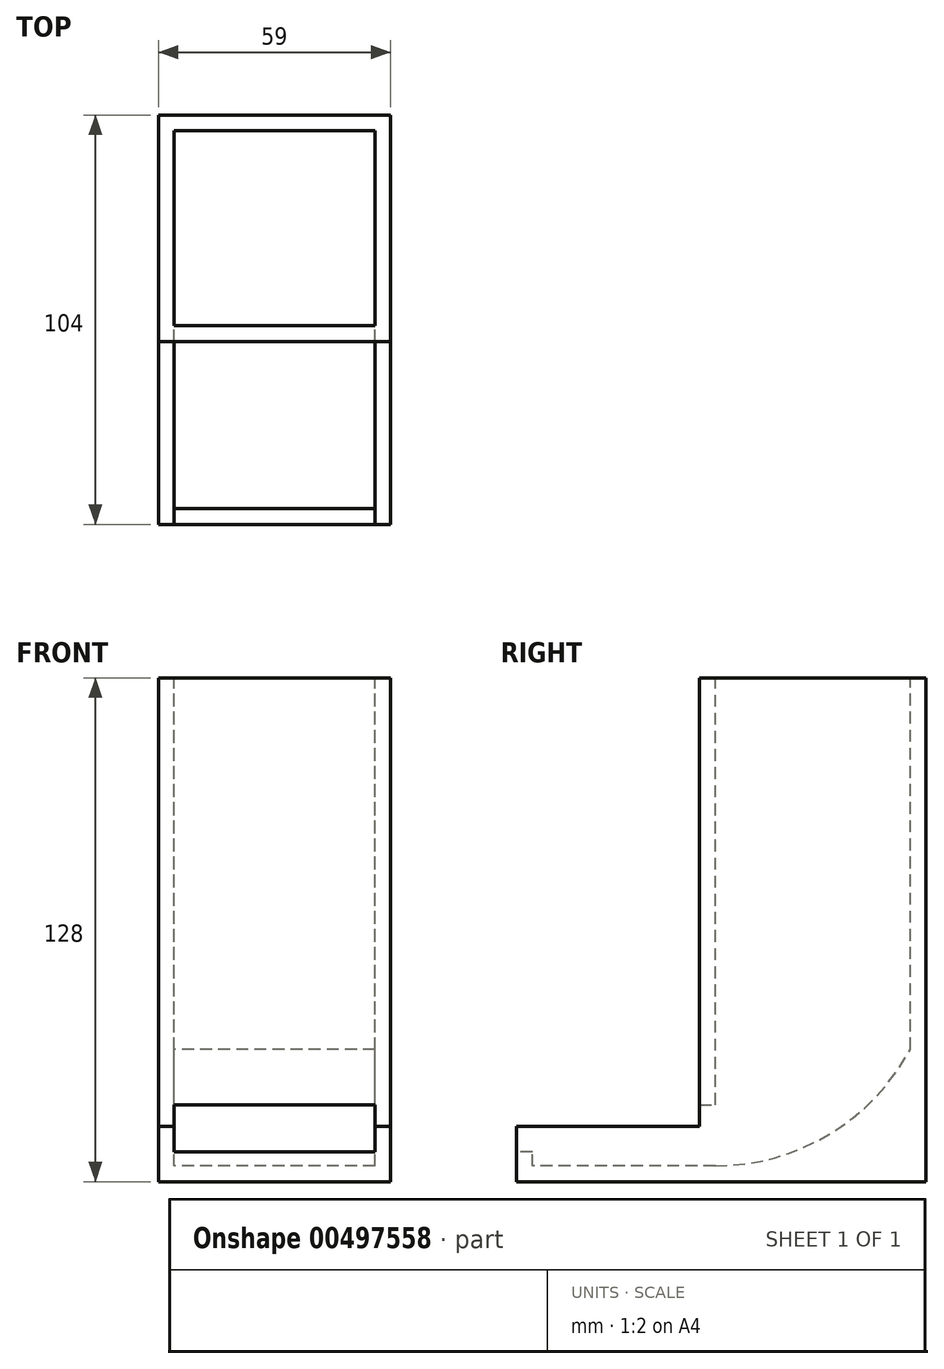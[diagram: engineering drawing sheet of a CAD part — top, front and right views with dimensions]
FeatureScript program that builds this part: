
annotation { "Feature Type Name" : "Feature", "Feature Type Description" : "" }
export const myFeature = defineFeature(function(context is Context, id is Id, definition is map)
    precondition{}
    {
        {
            var Q0;
            Q0=qCreatedBy(makeId("Right.planeOp"),FACE);
            var sketch = newSketch(context, id + "F0", { "sketchPlane" : qUnion([Q0])});
            skLineSegment(sketch, "E0", {"start": v(0, 0) * mm, "end": v(46.5, 0) * mm});
            skLineSegment(sketch, "E1", {"start": v(46.5, 0) * mm, "end": v(49.5, 0) * mm});
            skLineSegment(sketch, "E2", {"start": v(49.5, 0) * mm, "end": v(49.5, 120) * mm});
            skLineSegment(sketch, "E3", {"start": v(0, 0) * mm, "end": v(-46.5, 0) * mm});
            skLineSegment(sketch, "E4", {"start": v(-46.5, 0) * mm, "end": v(-46.5, 10) * mm});
            skLineSegment(sketch, "E5", {"start": v(-46.5, 10) * mm, "end": v(0, 10) * mm});
            skLineSegment(sketch, "E6", {"start": v(0, 15.5) * mm, "end": v(0, 120) * mm});
            skLineSegment(sketch, "E7", {"start": v(0, 120) * mm, "end": v(49.5, 120) * mm});
            skArc(sketch, "E8", {"start": v(0, 0) * mm, "mid": v(28.84, 7.97) * mm, "end": v(49.5, 29.6) * mm});
            skLineSegment(sketch, "E9", {"start": v(0, 0) * mm, "end": v(0, 10) * mm});
            skLineSegment(sketch, "E10", {"start": v(0, 15.5) * mm, "end": v(0, 56.18) * mm});
            skLineSegment(sketch, "E11", {"start": v(0, 10) * mm, "end": v(32, 10) * mm});
            skLineSegment(sketch, "E12.0", {"start": v(53.5, -4) * mm, "end": v(53.5, 124) * mm});
            skLineSegment(sketch, "E12.1", {"start": v(-4, 124) * mm, "end": v(53.5, 124) * mm});
            skLineSegment(sketch, "E12.2", {"start": v(-4, 15.5) * mm, "end": v(-4, 124) * mm});
            skLineSegment(sketch, "E13", {"start": v(-4, 15.5) * mm, "end": v(0, 15.5) * mm});
            skLineSegment(sketch, "E14.0", {"start": v(0, -4) * mm, "end": v(-50.5, -4) * mm});
            skLineSegment(sketch, "E14.1", {"start": v(0, -4) * mm, "end": v(46.5, -4) * mm});
            skLineSegment(sketch, "E14.2", {"start": v(46.5, -4) * mm, "end": v(53.5, -4) * mm});
            skLineSegment(sketch, "E15.0", {"start": v(-50.5, -4) * mm, "end": v(-50.5, 10) * mm});
            skLineSegment(sketch, "E16", {"start": v(-50.5, 10) * mm, "end": v(-46.5, 10) * mm});
            skLineSegment(sketch, "E17", {"start": v(-4, 15.5) * mm, "end": v(-4, 10) * mm});
            skLineSegment(sketch, "E18", {"start": v(-46.5, 3.51) * mm, "end": v(-50.5, 3.51) * mm});
            skLineSegment(sketch, "E19", {"start": v(0, 120) * mm, "end": v(0, 124) * mm});
            skLineSegment(sketch, "E20", {"start": v(49.5, 120) * mm, "end": v(49.5, 124) * mm});
            skSolve(sketch);
        }
        {
            var Q0;
            Q0=makeQuery(id+"F0.imprint","IMPRINT",FACE,{"disambiguationData":[TD([[makeQuery(id+"F0.imprint","IMPRINT",EDGE,{"derivedFrom":sQuery(id+"F0.wireOp",EDGE,"E0")}),-1.0]])]});
            var Q1;
            {var subQ4=sQuery(id+"F0.wireOp",EDGE,"E0");Q1=makeQuery(id+"F0.imprint","IMPRINT",FACE,{"disambiguationData":[TD([[makeQuery(id+"F0.imprint","IMPRINT",EDGE,{"derivedFrom":subQ4}),1.0]])]});}
            var Q2;
            {var subQ0=sQuery(id+"F0.wireOp",EDGE,"E9");Q2=makeQuery(id+"F0.imprint","IMPRINT",FACE,{"disambiguationData":[TD([[makeQuery(id+"F0.imprint","IMPRINT",EDGE,{"derivedFrom":subQ0}),-1.0]])]});}
            var Q3;
            Q3=makeQuery(id+"F0.imprint","IMPRINT",FACE,{"disambiguationData":[TD([[makeQuery(id+"F0.imprint","IMPRINT",EDGE,{"derivedFrom":sQuery(id+"F0.wireOp",EDGE,"E3")}),-1.0]])]});
            var Q4;
            Q4=makeQuery(id+"F0.imprint","IMPRINT",FACE,{"disambiguationData":[TD([[makeQuery(id+"F0.imprint","IMPRINT",EDGE,{"derivedFrom":sQuery(id+"F0.wireOp",EDGE,"E6")}),-1.0]])]});
            var Q5;
            {var subQ0=sQuery(id+"F0.wireOp",EDGE,"E16");Q5=makeQuery(id+"F0.imprint","IMPRINT",FACE,{"disambiguationData":[TD([[makeQuery(id+"F0.imprint","IMPRINT",EDGE,{"derivedFrom":subQ0}),-1.0]])]});}
            var Q6;
            Q6=makeQuery(id+"F0.imprint","IMPRINT",FACE,{"disambiguationData":[TD([[makeQuery(id+"F0.imprint","IMPRINT",EDGE,{"derivedFrom":sQuery(id+"F0.wireOp",EDGE,"E6")}),1.0]])]});
            var Q7;
            Q7=makeQuery(id+"F0.imprint","IMPRINT",FACE,{"disambiguationData":[TD([[makeQuery(id+"F0.imprint","IMPRINT",EDGE,{"derivedFrom":sQuery(id+"F0.wireOp",EDGE,"E7")}),1.0]])]});
            extrude(context, id + "F1", {"entities" : qUnion([Q0, Q1, Q2, Q3, Q4, Q5, Q6, Q7]), "oppositeDirection" : true, "depth" : 4 * mm, "offsetDistance" : 25 * mm});
        }
        {
            var Q0;
            Q0=makeQuery(id+"F0.imprint","IMPRINT",FACE,{"disambiguationData":[TD([[makeQuery(id+"F0.imprint","IMPRINT",EDGE,{"derivedFrom":sQuery(id+"F0.wireOp",EDGE,"E0")}),-1.0]])]});
            var Q1;
            {var subQ4=sQuery(id+"F0.wireOp",EDGE,"E0");Q1=makeQuery(id+"F0.imprint","IMPRINT",FACE,{"disambiguationData":[TD([[makeQuery(id+"F0.imprint","IMPRINT",EDGE,{"derivedFrom":subQ4}),1.0]])]});}
            var Q2;
            Q2=makeQuery(id+"F0.imprint","IMPRINT",FACE,{"disambiguationData":[TD([[makeQuery(id+"F0.imprint","IMPRINT",EDGE,{"derivedFrom":sQuery(id+"F0.wireOp",EDGE,"E6")}),-1.0]])]});
            var Q3;
            Q3=makeQuery(id+"F0.imprint","IMPRINT",FACE,{"disambiguationData":[TD([[makeQuery(id+"F0.imprint","IMPRINT",EDGE,{"derivedFrom":sQuery(id+"F0.wireOp",EDGE,"E3")}),-1.0]])]});
            var Q4;
            {var subQ0=sQuery(id+"F0.wireOp",EDGE,"E9");Q4=makeQuery(id+"F0.imprint","IMPRINT",FACE,{"disambiguationData":[TD([[makeQuery(id+"F0.imprint","IMPRINT",EDGE,{"derivedFrom":subQ0}),-1.0]])]});}
            var Q5;
            {var subQ0=sQuery(id+"F0.wireOp",EDGE,"E16");Q5=makeQuery(id+"F0.imprint","IMPRINT",FACE,{"disambiguationData":[TD([[makeQuery(id+"F0.imprint","IMPRINT",EDGE,{"derivedFrom":subQ0}),-1.0]])]});}
            var Q6;
            Q6=makeQuery(id+"F0.imprint","IMPRINT",FACE,{"disambiguationData":[TD([[makeQuery(id+"F0.imprint","IMPRINT",EDGE,{"derivedFrom":sQuery(id+"F0.wireOp",EDGE,"E6")}),1.0]])]});
            var Q7;
            Q7=makeQuery(id+"F0.imprint","IMPRINT",FACE,{"disambiguationData":[TD([[makeQuery(id+"F0.imprint","IMPRINT",EDGE,{"derivedFrom":sQuery(id+"F0.wireOp",EDGE,"E7")}),1.0]])]});
            extrude(context, id + "F2", {"entities" : qUnion([Q0, Q1, Q2, Q3, Q4, Q5, Q6, Q7]), "operationType" : NewBodyOperationType.ADD, "depth" : 55 * mm, "offsetDistance" : 25 * mm});
        }
        {
            var Q0;
            Q0=makeQuery(id+"F0.imprint","IMPRINT",FACE,{"disambiguationData":[TD([[makeQuery(id+"F0.imprint","IMPRINT",EDGE,{"derivedFrom":sQuery(id+"F0.wireOp",EDGE,"E6")}),-1.0]])]});
            var Q1;
            {var subQ0=sQuery(id+"F0.wireOp",EDGE,"E9");Q1=makeQuery(id+"F0.imprint","IMPRINT",FACE,{"disambiguationData":[TD([[makeQuery(id+"F0.imprint","IMPRINT",EDGE,{"derivedFrom":subQ0}),-1.0]])]});}
            var Q2;
            {var subQ5=sQuery(id+"F0.wireOp",EDGE,"E3");Q2=makeQuery(id+"F0.imprint","IMPRINT",FACE,{"disambiguationData":[TD([[makeQuery(id+"F0.imprint","IMPRINT",EDGE,{"derivedFrom":subQ5}),-1.0]])]});}
            var Q3;
            {var subQ0=sQuery(id+"F0.wireOp",EDGE,"E16");Q3=makeQuery(id+"F0.imprint","IMPRINT",FACE,{"disambiguationData":[TD([[makeQuery(id+"F0.imprint","IMPRINT",EDGE,{"derivedFrom":subQ0}),-1.0]])]});}
            var Q4;
            Q4=makeQuery(id+"F0.imprint","IMPRINT",FACE,{"disambiguationData":[TD([[makeQuery(id+"F0.imprint","IMPRINT",EDGE,{"derivedFrom":sQuery(id+"F0.wireOp",EDGE,"E7")}),1.0]])]});
            extrude(context, id + "F3", {"entities" : qUnion([Q0, Q1, Q2, Q3, Q4]), "operationType" : NewBodyOperationType.REMOVE, "depth" : 51 * mm, "offsetDistance" : 25 * mm});
        }
    });
